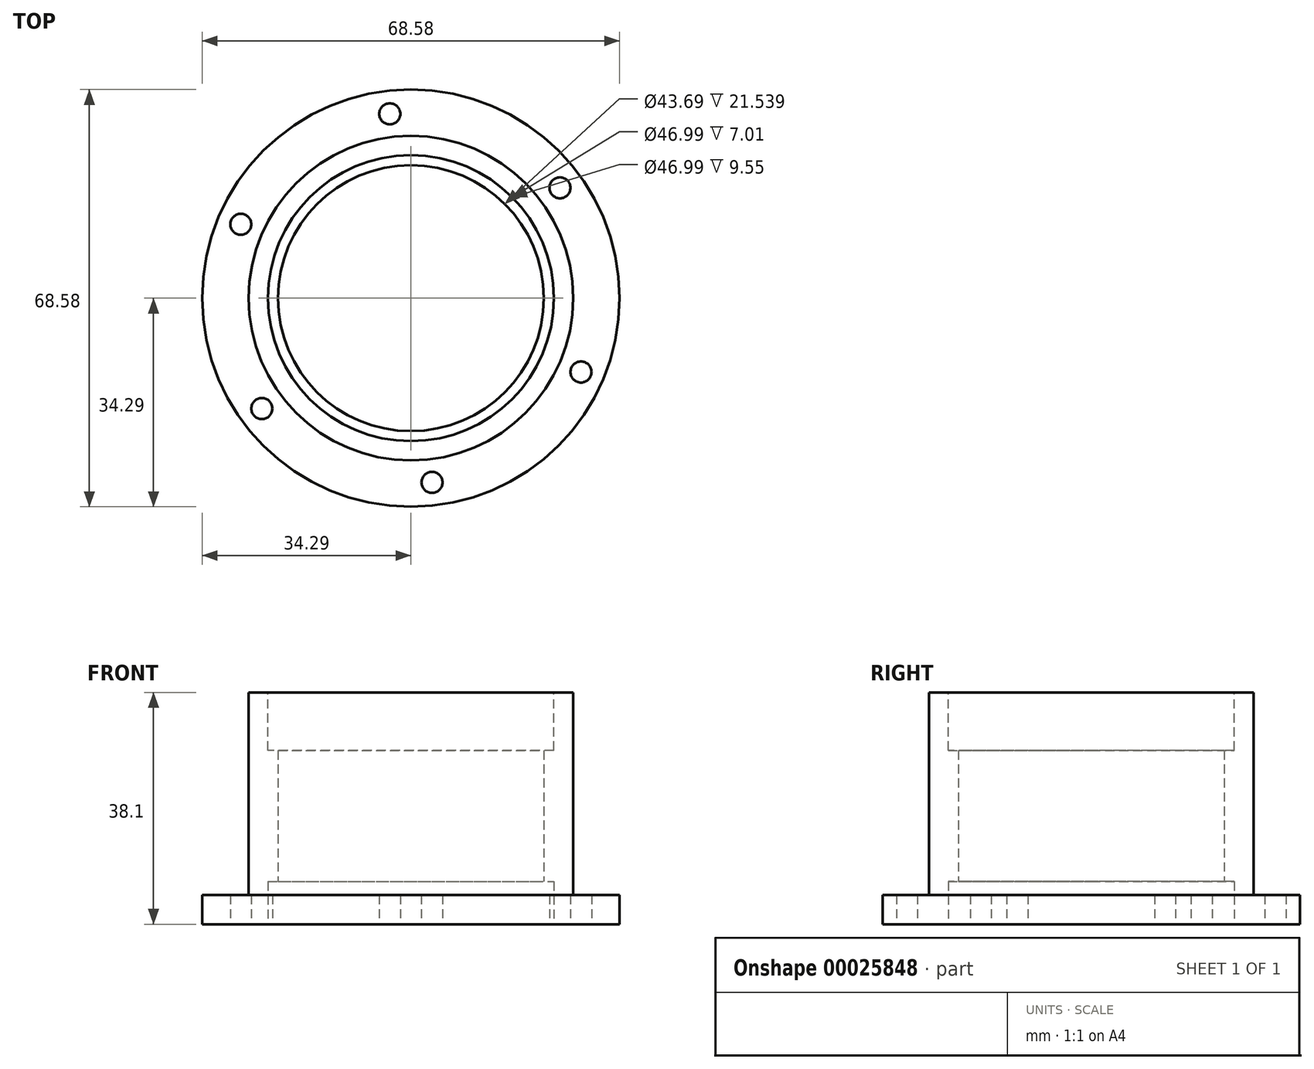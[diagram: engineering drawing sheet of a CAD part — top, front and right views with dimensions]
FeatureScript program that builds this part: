
annotation { "Feature Type Name" : "Feature", "Feature Type Description" : "" }
export const myFeature = defineFeature(function(context is Context, id is Id, definition is map)
    precondition{}
    {
        {
            var Q0;
            Q0=qCreatedBy(makeId("Front.planeOp"),FACE);
            var sketch = newSketch(context, id + "F0", { "sketchPlane" : qUnion([Q0])});
            skLineSegment(sketch, "E0", {"start": v(0, 19.05) * mm, "end": v(0, -19.05) * mm});
            skLineSegment(sketch, "E1", {"start": v(0, -19.05) * mm, "end": v(34.3, -19.05) * mm});
            skLineSegment(sketch, "E2", {"start": v(34.3, -19.05) * mm, "end": v(34.3, -14.27) * mm});
            skLineSegment(sketch, "E3", {"start": v(34.3, -14.27) * mm, "end": v(26.67, -14.27) * mm});
            skLineSegment(sketch, "E4", {"start": v(26.67, -14.27) * mm, "end": v(26.67, 19.05) * mm});
            skLineSegment(sketch, "E5", {"start": v(26.67, 19.05) * mm, "end": v(0, 19.05) * mm});
            skLineSegment(sketch, "E6", {"start": v(0, 52.98) * mm, "end": v(0, -67.36) * mm, "construction": true});
            skLineSegment(sketch, "E7", {"start": v(-34.07, 0) * mm, "end": v(83.84, 0) * mm, "construction": true});
            skSolve(sketch);
        }
        {
            var Q0;
            Q0=makeQuery(id+"F0.imprint","IMPRINT",FACE,{"disambiguationData":[TD([[makeQuery(id+"F0.imprint","IMPRINT",EDGE,{"derivedFrom":sQuery(id+"F0.wireOp",EDGE,"E0")}),1.0]])]});
            var Q1;
            Q1=sQuery(id+"F0.wireOp",EDGE,"E6");
            revolve(context, id + "F1", {"entities" : qUnion([Q0]), "axis" : qUnion([Q1]), "revolveType" : RevolveType.FULL});
        }
        {
            var Q0;
            Q0=makeQuery(id+"F1.opRevolve","SWEPT_FACE",FACE,{"disambiguationData":[OSD([sQuery(id+"F0.wireOp",EDGE,"E1")])]});
            var sketch = newSketch(context, id + "F2", { "sketchPlane" : qUnion([Q0])});
            skCircle(sketch, "E8", {"center": v(0, 0) * mm, "radius": 30.48 * mm});
            skCircle(sketch, "E9.cCircle", {"center": v(0, 0) * mm, "radius": 30.48 * mm, "construction": true});
            skLineSegment(sketch, "E9.0", {"start": v(24.5, -18.14) * mm, "end": v(-3.46, -30.28) * mm});
            skLineSegment(sketch, "E9.1", {"start": v(-3.46, -30.28) * mm, "end": v(-27.96, -12.14) * mm});
            skLineSegment(sketch, "E9.2", {"start": v(-27.96, -12.14) * mm, "end": v(-24.5, 18.14) * mm});
            skLineSegment(sketch, "E9.3", {"start": v(-24.5, 18.14) * mm, "end": v(3.46, 30.28) * mm});
            skLineSegment(sketch, "E9.4", {"start": v(3.46, 30.28) * mm, "end": v(27.96, 12.14) * mm});
            skLineSegment(sketch, "E9.5", {"start": v(27.96, 12.14) * mm, "end": v(24.5, -18.14) * mm});
            skSolve(sketch);
        }
        {
            var Q0;
            Q0=sQuery(id+"F2.wireOp",VERTEX,"E9.4.start");
            var Q1;
            Q1=sQuery(id+"F2.wireOp",VERTEX,"E9.3.start");
            var Q2;
            Q2=sQuery(id+"F2.wireOp",VERTEX,"E9.2.start");
            var Q3;
            Q3=sQuery(id+"F2.wireOp",VERTEX,"E9.1.start");
            var Q4;
            Q4=sQuery(id+"F2.wireOp",VERTEX,"E9.0.start");
            var Q5;
            Q5=sQuery(id+"F2.wireOp",VERTEX,"E9.5.start");
            var Q6;
            Q6=makeQuery(id+"F1.opRevolve","SWEPT_BODY",BODY,{"disambiguationData":[OSD([sQuery(id+"F0.wireOp",EDGE,"E0"),sQuery(id+"F0.wireOp",EDGE,"E1"),sQuery(id+"F0.wireOp",EDGE,"E2"),sQuery(id+"F0.wireOp",EDGE,"E3"),sQuery(id+"F0.wireOp",EDGE,"E4"),sQuery(id+"F0.wireOp",EDGE,"E5")])]});
            hole(context, id + "F3", {"style" : HoleStyle.SIMPLE, "holeDiameter" : 3.45 * mm, "endStyle" : HoleEndStyle.THROUGH, "locations" : qUnion([Q0, Q1, Q2, Q3, Q4, Q5]), "scope" : qUnion([Q6])});
        }
        {
            var Q0;
            Q0=makeQuery(id+"F1.opRevolve","SWEPT_FACE",FACE,{"disambiguationData":[OSD([sQuery(id+"F0.wireOp",EDGE,"E1")])]});
            var sketch = newSketch(context, id + "F4", { "sketchPlane" : qUnion([Q0])});
            skCircle(sketch, "E10", {"center": v(0, 0) * mm, "radius": 23.5 * mm});
            skCircle(sketch, "E11", {"center": v(0, 0) * mm, "radius": 21.84 * mm});
            skSolve(sketch);
        }
        {
            var Q0;
            Q0=makeQuery(id+"F4.imprint","IMPRINT",FACE,{"disambiguationData":[TD([[makeQuery(id+"F4.imprint","IMPRINT",EDGE,{"derivedFrom":sQuery(id+"F4.wireOp",EDGE,"E11")}),1.0]])]});
            extrude(context, id + "F5", {"entities" : qUnion([Q0]), "operationType" : NewBodyOperationType.REMOVE, "endBound" : BoundingType.THROUGH_ALL, "oppositeDirection" : true, "depth" : 7 * mm});
        }
        {
            var Q0;
            Q0=makeQuery(id+"F1.opRevolve","SWEPT_FACE",FACE,{"disambiguationData":[OSD([sQuery(id+"F0.wireOp",EDGE,"E1")])]});
            var sketch = newSketch(context, id + "F6", { "sketchPlane" : qUnion([Q0])});
            skCircle(sketch, "E12", {"center": v(0, 0) * mm, "radius": 23.5 * mm});
            skSolve(sketch);
        }
        {
            var Q0;
            Q0=makeQuery(id+"F6.imprint","IMPRINT",FACE,{"disambiguationData":[TD([[makeQuery(id+"F6.imprint","IMPRINT",EDGE,{"derivedFrom":sQuery(id+"F6.wireOp",EDGE,"E12")}),1.0]])]});
            extrude(context, id + "F7", {"entities" : qUnion([Q0]), "operationType" : NewBodyOperationType.REMOVE, "oppositeDirection" : true, "depth" : 7 * mm});
        }
        {
            var Q0;
            Q0=makeQuery(id+"F1.opRevolve","SWEPT_FACE",FACE,{"disambiguationData":[OSD([sQuery(id+"F0.wireOp",EDGE,"E5")])]});
            var sketch = newSketch(context, id + "F8", { "sketchPlane" : qUnion([Q0])});
            skCircle(sketch, "E13", {"center": v(0, 0) * mm, "radius": 23.5 * mm});
            skSolve(sketch);
        }
        {
            var Q0;
            Q0=makeQuery(id+"F8.imprint","IMPRINT",FACE,{"disambiguationData":[TD([[makeQuery(id+"F8.imprint","IMPRINT",EDGE,{"derivedFrom":sQuery(id+"F8.wireOp",EDGE,"E13")}),1.0]])]});
            extrude(context, id + "F9", {"entities" : qUnion([Q0]), "operationType" : NewBodyOperationType.REMOVE, "oppositeDirection" : true, "depth" : 9.55 * mm});
        }
    });
